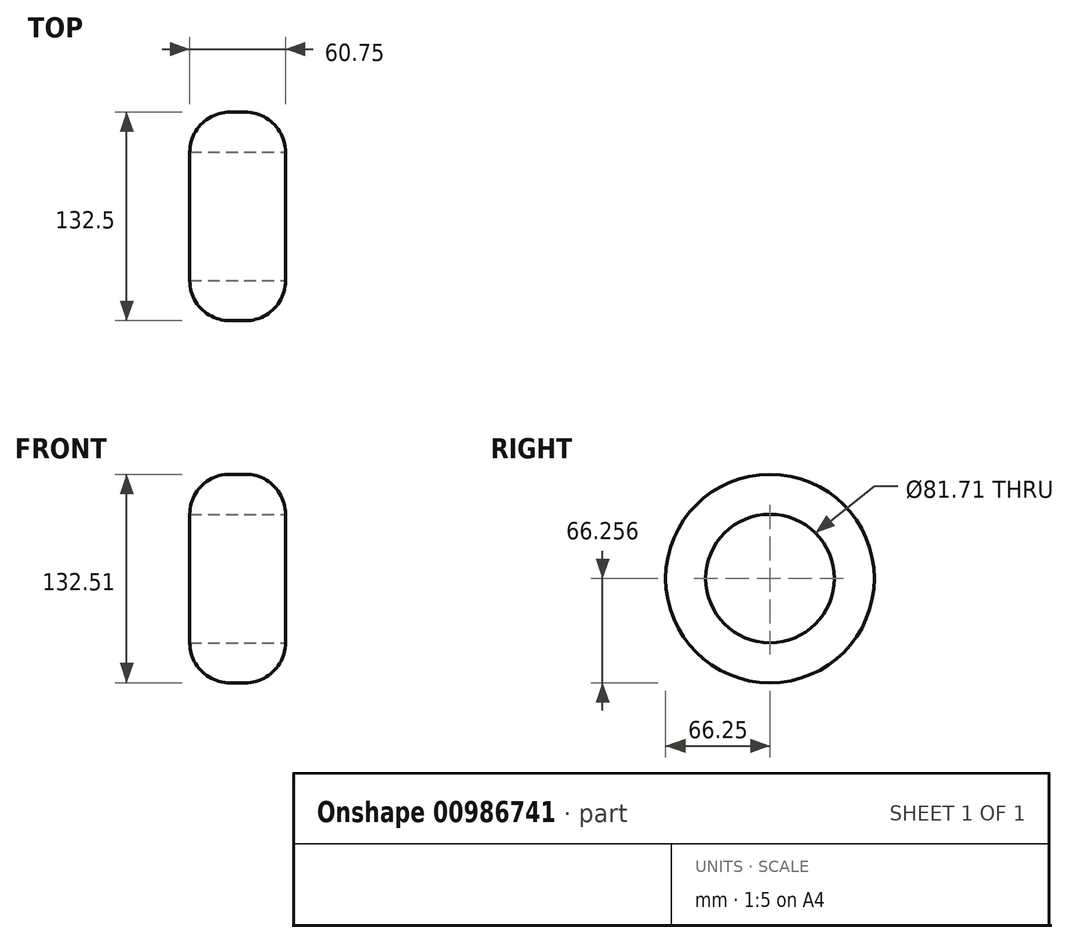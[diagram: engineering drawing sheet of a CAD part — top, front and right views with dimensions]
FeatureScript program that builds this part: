
annotation { "Feature Type Name" : "Feature", "Feature Type Description" : "" }
export const myFeature = defineFeature(function(context is Context, id is Id, definition is map)
    precondition{}
    {
        {
            var Q0;
            Q0=qCreatedBy(makeId("Front.planeOp"),FACE);
            var sketch = newSketch(context, id + "F0", { "sketchPlane" : qUnion([Q0])});
            skLineSegment(sketch, "E0.bottom", {"start": v(-29, 36.57) * mm, "end": v(31.75, 36.57) * mm});
            skLineSegment(sketch, "E0.top", {"start": v(-29, -29.69) * mm, "end": v(31.75, -29.69) * mm});
            skLineSegment(sketch, "E0.left", {"start": v(-29, 36.57) * mm, "end": v(-29, -29.69) * mm});
            skLineSegment(sketch, "E0.right", {"start": v(31.75, 36.57) * mm, "end": v(31.75, -29.69) * mm});
            skSolve(sketch);
        }
        {
            var Q0;
            Q0=makeQuery(id+"F0.imprint","IMPRINT",FACE,{"disambiguationData":[TD([[makeQuery(id+"F0.imprint","IMPRINT",EDGE,{"derivedFrom":sQuery(id+"F0.wireOp",EDGE,"E0.bottom")}),-1.0]])]});
            var Q1;
            Q1=sQuery(id+"F0.wireOp",EDGE,"E0.bottom");
            revolve(context, id + "F1", {"surfaceOperationType" : NewSurfaceOperationType.NEW, "entities" : qUnion([Q0]), "axis" : qUnion([Q1]), "revolveType" : RevolveType.FULL});
        }
        {
            var Q0;
            Q0=makeQuery(id+"F1.opRevolve","SWEPT_EDGE",EDGE,{"disambiguationData":[OSD([sQuery(id+"F0.wireOp",EDGE,"E0.top"),sQuery(id+"F0.wireOp",EDGE,"E0.right")])]});
            var Q1;
            Q1=makeQuery(id+"F1.opRevolve","SWEPT_EDGE",EDGE,{"disambiguationData":[OSD([sQuery(id+"F0.wireOp",EDGE,"E0.top"),sQuery(id+"F0.wireOp",EDGE,"E0.left")])]});
            fillet(context, id + "F2", {"entities" : qUnion([Q0, Q1]), "radius" : 25.4 * mm, "tangentPropagation" : true, "allowEdgeOverflow" : false});
        }
        {
            var Q0;
            Q0=makeQuery(id+"F1.opRevolve","SWEPT_FACE",FACE,{"disambiguationData":[OSD([sQuery(id+"F0.wireOp",EDGE,"E0.right")])]});
            extrude(context, id + "F3", {"entities" : qUnion([Q0]), "operationType" : NewBodyOperationType.REMOVE, "oppositeDirection" : true, "depth" : 127 * mm, "offsetDistance" : 25.4 * mm});
        }
    });
